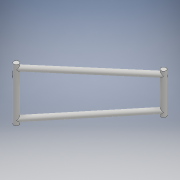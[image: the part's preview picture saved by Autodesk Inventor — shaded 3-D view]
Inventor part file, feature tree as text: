
AUTODESK INVENTOR PART (.ipt)
format: ipt  version: 2019.3 (Build 233278000, 278)  size: 218,112 bytes
history: native  units: mm
features: other x8, plane x8, sketch x8, extrude x7, reference x7, shell x1, mirror x1, projected_geometry x1
ambient origin geometry x8: Origin, YZ Plane, XZ Plane, XY Plane, X Axis, Y Axis, Z Axis, Center Point
bodies: Body1 (feature_tree), Body2 (feature_tree), Body3 (feature_tree)
feature tree (41):
  other  "BaseCage"
  plane  "Work Plane1"
  sketch  "Sketch1"  dims[d0=15.875mm d1=10.0mm d2=0.0mm]
  plane  "Work Plane2"
  extrude  "Extrusion1"  Depth=10.0mm TaperAngle=0.0deg
  plane  "Work Plane3"
  sketch  "Sketch2"  dims[d3=15.875mm d4=10.0mm d5=0.0mm d6=1.6mm]
  plane  "Work Plane4"
  extrude  "Extrusion2"  Depth=10.0mm TaperAngle=0.0deg
  shell  "Shell1"  Thickness=1.6mm
  sketch  "3D Sketch1"
  plane  "Work Plane5"
  extrude  "Extrusion3"  Depth=14.0mm
  mirror  "Mirror1"
  extrude  "Extrusion4"  Depth=1.6mm
  extrude  "Extrusion5"  Depth=10.0mm TaperAngle=0.0deg
  plane  "Work Plane7"
  plane  "Work Plane14"
  plane  "Work Plane15"
  sketch  "Sketch6"  dims[d15=10.0mm d16=0.0mm d19=4.0mm]
  extrude  "Extrusion8"  Depth=10.0mm
  extrude  "Extrusion10"  Depth=4.0mm
  reference  "Reference1"
  reference  "Reference2"
  sketch  "Sketch3"  dims[d7=14.0mm d8=14.0mm]
  sketch  "Sketch4"  dims[d9=15.875mm d10=1.6mm]
  reference  "Reference3"
  sketch  "Sketch5"  dims[d11=10.0mm d12=0.0mm d13=10.0mm d14=0.0mm]
  reference  "Reference4"
  projected_geometry  "Projected Loop1"
  other  "TabRear"
  sketch  "Sketch12"  dims[d23=3.0mm d24=0.0mm d27=4.0mm d28=3.0mm d29=0.0mm]
  reference  "Reference7"
  reference  "Reference8"
  reference  "Reference9"
  other  "TabFront"
  other  "<userpath>\Desktop\3dprojects\OpenEmoto\MainFrame\Battery\Assembly.iam"
  other  "Assembly.iam"
  other  "MainFrame:1"
  other  "PlateRight:1"
  other  "Assembly4"
